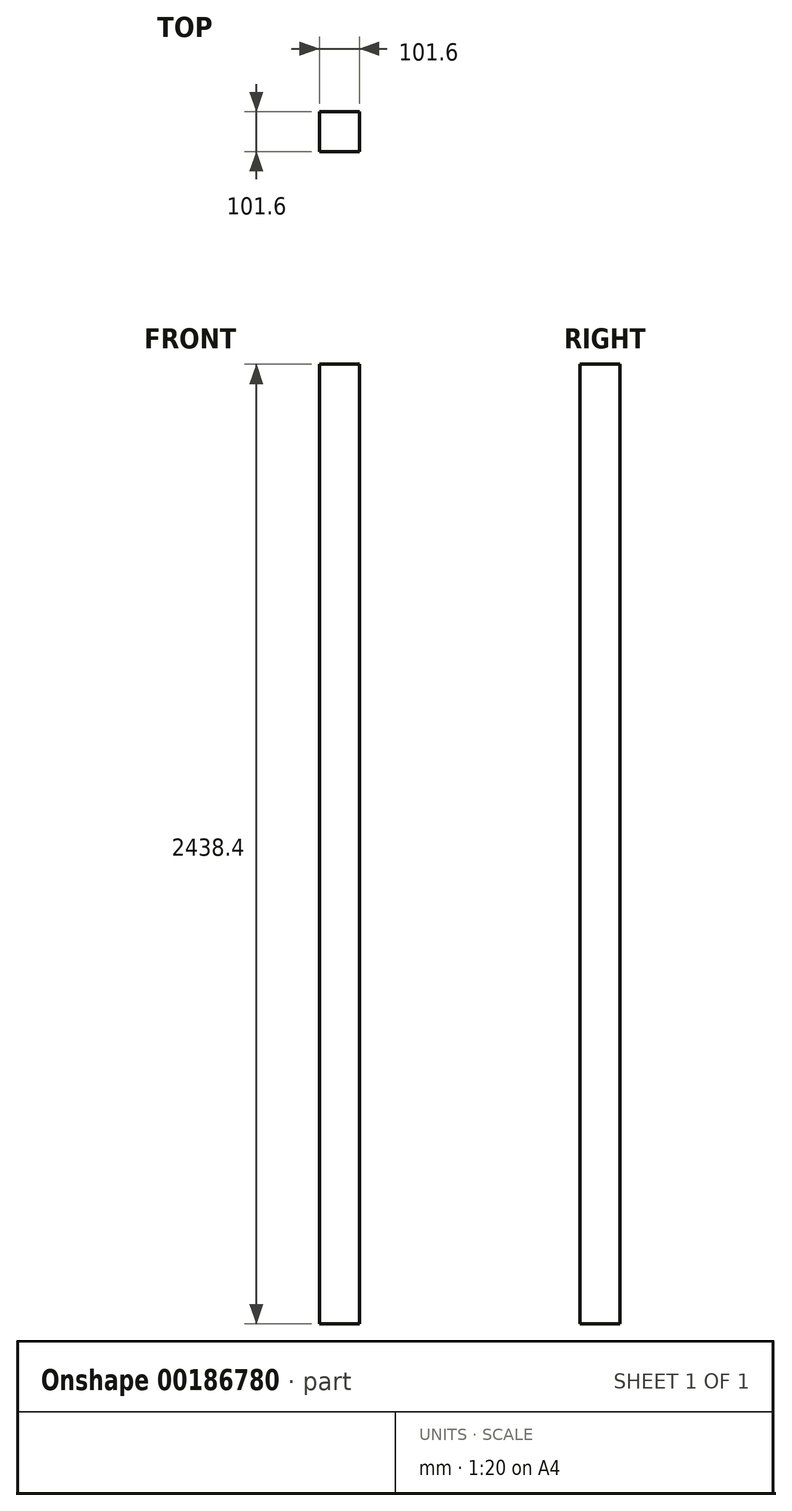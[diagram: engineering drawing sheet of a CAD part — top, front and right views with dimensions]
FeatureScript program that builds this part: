
annotation { "Feature Type Name" : "Feature", "Feature Type Description" : "" }
export const myFeature = defineFeature(function(context is Context, id is Id, definition is map)
    precondition{}
    {
        {
            var Q0;
            Q0=qCreatedBy(makeId("Top.planeOp"),FACE);
            var sketch = newSketch(context, id + "F0", { "sketchPlane" : qUnion([Q0])});
            skLineSegment(sketch, "E0.bottom", {"start": v(-50.8, 50.8) * mm, "end": v(50.8, 50.8) * mm});
            skLineSegment(sketch, "E0.top", {"start": v(-50.8, -50.8) * mm, "end": v(50.8, -50.8) * mm});
            skLineSegment(sketch, "E0.left", {"start": v(-50.8, 50.8) * mm, "end": v(-50.8, -50.8) * mm});
            skLineSegment(sketch, "E0.right", {"start": v(50.8, 50.8) * mm, "end": v(50.8, -50.8) * mm});
            skPoint(sketch, "E0.middle", {"position": v(0, 0) * mm});
            skSolve(sketch);
        }
        {
            var Q0;
            Q0 = qSketchRegion(id + "F0", true);
            extrude(context, id + "F1", {"entities" : qUnion([Q0]), "depth" : 2438.4 * mm});
        }
    });
